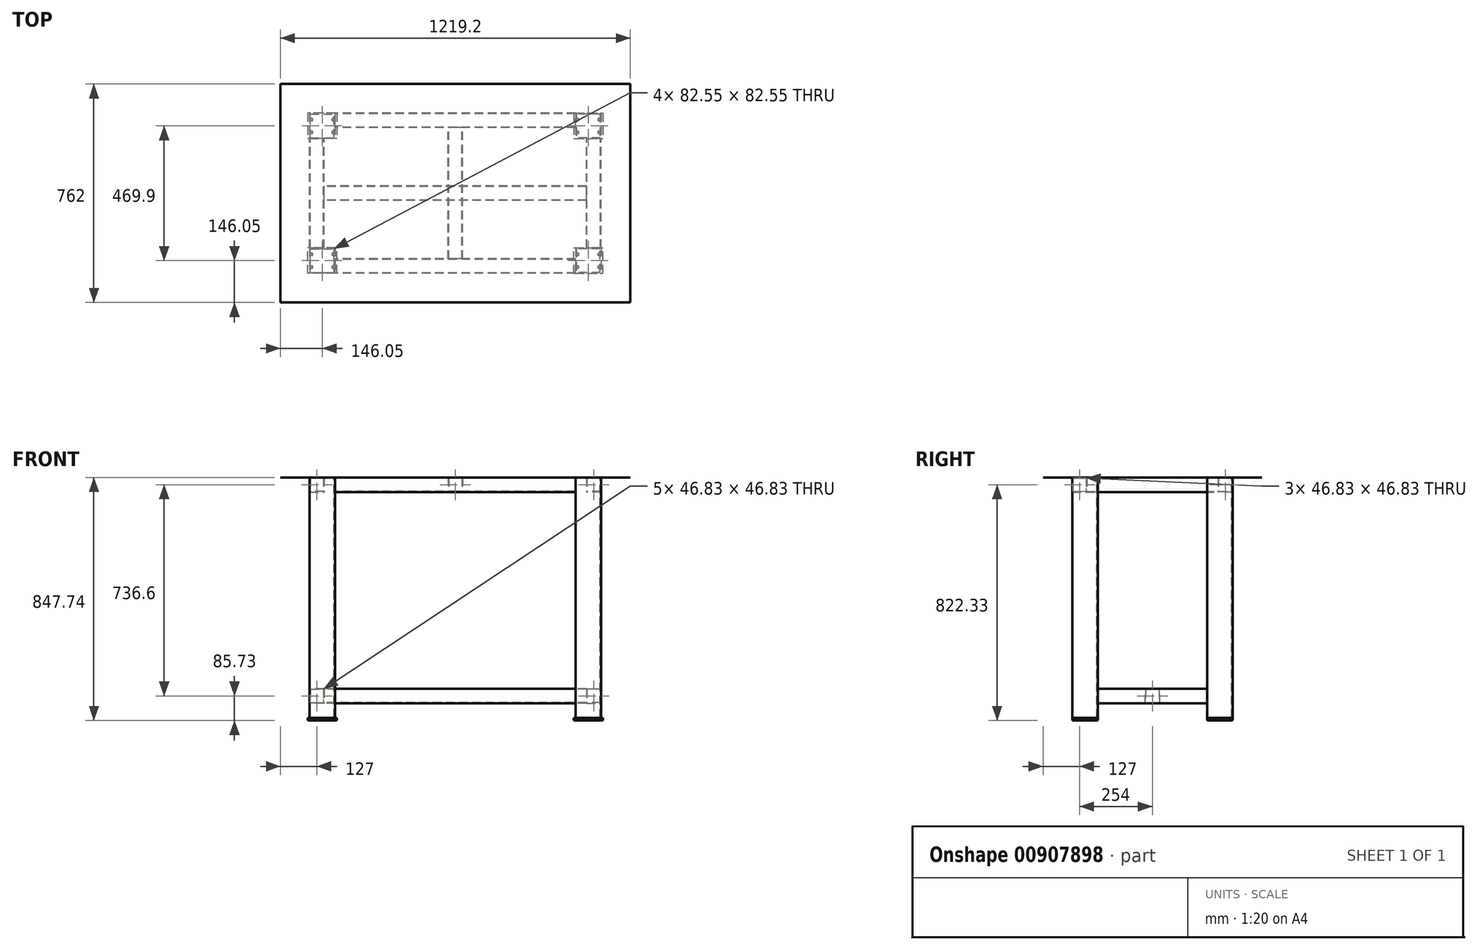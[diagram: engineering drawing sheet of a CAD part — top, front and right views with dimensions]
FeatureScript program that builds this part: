
annotation { "Feature Type Name" : "Feature", "Feature Type Description" : "" }
export const myFeature = defineFeature(function(context is Context, id is Id, definition is map)
    precondition{}
    {
        {
            var Q0;
            Q0=qCreatedBy(makeId("Top.planeOp"),FACE);
            var sketch = newSketch(context, id + "F0", { "sketchPlane" : qUnion([Q0])});
            skLineSegment(sketch, "E0.bottom", {"start": v(-419.1, 279.4) * mm, "end": v(-508, 279.4) * mm});
            skLineSegment(sketch, "E0.top", {"start": v(-419.1, 190.5) * mm, "end": v(-508, 190.5) * mm});
            skLineSegment(sketch, "E0.left", {"start": v(-419.1, 279.4) * mm, "end": v(-419.1, 190.5) * mm});
            skLineSegment(sketch, "E0.right", {"start": v(-508, 279.4) * mm, "end": v(-508, 190.5) * mm});
            skPoint(sketch, "E0.middle", {"position": v(-463.55, 234.95) * mm});
            skLineSegment(sketch, "E1.bottom", {"start": v(-419.1, -190.5) * mm, "end": v(-508, -190.5) * mm});
            skLineSegment(sketch, "E1.top", {"start": v(-419.1, -279.4) * mm, "end": v(-508, -279.4) * mm});
            skLineSegment(sketch, "E1.left", {"start": v(-419.1, -190.5) * mm, "end": v(-419.1, -279.4) * mm});
            skLineSegment(sketch, "E1.right", {"start": v(-508, -190.5) * mm, "end": v(-508, -279.4) * mm});
            skPoint(sketch, "E1.middle", {"position": v(-463.55, -234.95) * mm});
            skPoint(sketch, "E2.MirrorP", {"position": v(463.55, -234.95) * mm});
            skLineSegment(sketch, "E3.MirrorCS", {"start": v(419.1, 190.5) * mm, "end": v(508, 190.5) * mm});
            skLineSegment(sketch, "E4.MirrorCS", {"start": v(419.1, -190.5) * mm, "end": v(419.1, -279.4) * mm});
            skLineSegment(sketch, "E5.MirrorCS", {"start": v(419.1, 279.4) * mm, "end": v(419.1, 190.5) * mm});
            skLineSegment(sketch, "E6.MirrorCS", {"start": v(419.1, 279.4) * mm, "end": v(508, 279.4) * mm});
            skPoint(sketch, "E7.MirrorP", {"position": v(463.55, 234.95) * mm});
            skLineSegment(sketch, "E8.MirrorCS", {"start": v(419.1, -190.5) * mm, "end": v(508, -190.5) * mm});
            skLineSegment(sketch, "E9.MirrorCS", {"start": v(508, 279.4) * mm, "end": v(508, 190.5) * mm});
            skLineSegment(sketch, "E10.MirrorCS", {"start": v(419.1, -279.4) * mm, "end": v(508, -279.4) * mm});
            skLineSegment(sketch, "E11.MirrorCS", {"start": v(508, -190.5) * mm, "end": v(508, -279.4) * mm});
            skLineSegment(sketch, "E12.bottom", {"start": v(-504.83, 193.67) * mm, "end": v(-422.28, 193.67) * mm});
            skLineSegment(sketch, "E12.top", {"start": v(-504.83, 276.23) * mm, "end": v(-422.28, 276.23) * mm});
            skLineSegment(sketch, "E12.left", {"start": v(-504.83, 193.67) * mm, "end": v(-504.83, 276.23) * mm});
            skLineSegment(sketch, "E12.right", {"start": v(-422.28, 193.67) * mm, "end": v(-422.28, 276.23) * mm});
            skLineSegment(sketch, "E13.bottom", {"start": v(-504.83, -276.23) * mm, "end": v(-422.27, -276.23) * mm});
            skLineSegment(sketch, "E13.top", {"start": v(-504.83, -193.68) * mm, "end": v(-422.27, -193.68) * mm});
            skLineSegment(sketch, "E13.left", {"start": v(-504.83, -276.23) * mm, "end": v(-504.83, -193.68) * mm});
            skLineSegment(sketch, "E13.right", {"start": v(-422.27, -276.23) * mm, "end": v(-422.27, -193.68) * mm});
            skLineSegment(sketch, "E14.MirrorCS", {"start": v(-419.1, 190.5) * mm, "end": v(-419.1, 279.4) * mm});
            skLineSegment(sketch, "E15.MirrorCS", {"start": v(-504.83, 193.68) * mm, "end": v(-422.27, 193.68) * mm});
            skLineSegment(sketch, "E16.MirrorCS", {"start": v(-504.83, 276.23) * mm, "end": v(-422.27, 276.23) * mm});
            skLineSegment(sketch, "E17.MirrorCS", {"start": v(-504.83, 276.23) * mm, "end": v(-504.83, 193.68) * mm});
            skLineSegment(sketch, "E18.MirrorCS", {"start": v(-508, 190.5) * mm, "end": v(-508, 279.4) * mm});
            skLineSegment(sketch, "E19.MirrorCS", {"start": v(-422.27, 276.23) * mm, "end": v(-422.27, 193.68) * mm});
            skLineSegment(sketch, "E20.MirrorCS", {"start": v(-419.1, -279.4) * mm, "end": v(-419.1, -190.5) * mm});
            skLineSegment(sketch, "E21.MirrorCS", {"start": v(-422.28, -193.67) * mm, "end": v(-422.28, -276.23) * mm});
            skLineSegment(sketch, "E22.MirrorCS", {"start": v(504.83, 193.67) * mm, "end": v(422.28, 193.67) * mm});
            skLineSegment(sketch, "E23.MirrorCS", {"start": v(508, 190.5) * mm, "end": v(508, 279.4) * mm});
            skLineSegment(sketch, "E24.MirrorCS", {"start": v(422.28, -193.67) * mm, "end": v(422.28, -276.23) * mm});
            skLineSegment(sketch, "E25.MirrorCS", {"start": v(419.1, -279.4) * mm, "end": v(419.1, -190.5) * mm});
            skLineSegment(sketch, "E26.MirrorCS", {"start": v(504.83, 193.68) * mm, "end": v(422.27, 193.68) * mm});
            skLineSegment(sketch, "E27.MirrorCS", {"start": v(419.1, 190.5) * mm, "end": v(419.1, 279.4) * mm});
            skLineSegment(sketch, "E28.MirrorCS", {"start": v(504.83, -193.68) * mm, "end": v(422.27, -193.68) * mm});
            skLineSegment(sketch, "E29.MirrorCS", {"start": v(504.83, 276.23) * mm, "end": v(422.27, 276.23) * mm});
            skLineSegment(sketch, "E30.MirrorCS", {"start": v(422.27, -276.23) * mm, "end": v(422.27, -193.68) * mm});
            skLineSegment(sketch, "E31.MirrorCS", {"start": v(422.27, 276.23) * mm, "end": v(422.27, 193.68) * mm});
            skLineSegment(sketch, "E32.MirrorCS", {"start": v(504.83, 276.23) * mm, "end": v(504.83, 193.68) * mm});
            skLineSegment(sketch, "E33.MirrorCS", {"start": v(504.83, -276.23) * mm, "end": v(422.27, -276.23) * mm});
            skLineSegment(sketch, "E34.MirrorCS", {"start": v(422.28, 193.67) * mm, "end": v(422.28, 276.23) * mm});
            skLineSegment(sketch, "E35.MirrorCS", {"start": v(504.83, 193.67) * mm, "end": v(504.83, 276.23) * mm});
            skLineSegment(sketch, "E36.MirrorCS", {"start": v(504.83, 276.23) * mm, "end": v(422.28, 276.23) * mm});
            skLineSegment(sketch, "E37.MirrorCS", {"start": v(504.83, -276.23) * mm, "end": v(504.83, -193.68) * mm});
            skSolve(sketch);
        }
        {
            var Q0;
            Q0=makeQuery(id+"F0.imprint","IMPRINT",FACE,{"disambiguationData":[TD([[makeQuery(id+"F0.imprint","IMPRINT",EDGE,{"derivedFrom":sQuery(id+"F0.wireOp",EDGE,"E28.MirrorCS")}),-1.0]])]});
            var Q1;
            Q1=makeQuery(id+"F0.imprint","IMPRINT",FACE,{"disambiguationData":[TD([[makeQuery(id+"F0.imprint","IMPRINT",EDGE,{"derivedFrom":sQuery(id+"F0.wireOp",EDGE,"E26.MirrorCS")}),1.0]])]});
            var Q2;
            Q2=makeQuery(id+"F0.imprint","IMPRINT",FACE,{"disambiguationData":[TD([[makeQuery(id+"F0.imprint","IMPRINT",EDGE,{"derivedFrom":sQuery(id+"F0.wireOp",EDGE,"E1.top")}),-1.0]])]});
            var Q3;
            Q3=makeQuery(id+"F0.imprint","IMPRINT",FACE,{"disambiguationData":[TD([[makeQuery(id+"F0.imprint","IMPRINT",EDGE,{"derivedFrom":sQuery(id+"F0.wireOp",EDGE,"E15.MirrorCS")}),-1.0]])]});
            extrude(context, id + "F1", {"entities" : qUnion([Q0, Q1, Q2, Q3]), "oppositeDirection" : true, "depth" : 838.2 * mm, "offsetDistance" : 25.4 * mm});
        }
        {
            var Q0;
            Q0=qCreatedBy(makeId("Right.planeOp"),FACE);
            var sketch = newSketch(context, id + "F2", { "sketchPlane" : qUnion([Q0])});
            skLineSegment(sketch, "E38.bottom", {"start": v(-279.4, 0) * mm, "end": v(-228.6, 0) * mm});
            skLineSegment(sketch, "E38.top", {"start": v(-279.4, -50.8) * mm, "end": v(-228.6, -50.8) * mm});
            skLineSegment(sketch, "E38.left", {"start": v(-279.4, 0) * mm, "end": v(-279.4, -50.8) * mm});
            skLineSegment(sketch, "E38.right", {"start": v(-228.6, 0) * mm, "end": v(-228.6, -50.8) * mm});
            skLineSegment(sketch, "E39.bottom", {"start": v(279.4, 0) * mm, "end": v(228.6, 0) * mm});
            skLineSegment(sketch, "E39.top", {"start": v(279.4, -50.8) * mm, "end": v(228.6, -50.8) * mm});
            skLineSegment(sketch, "E39.left", {"start": v(228.6, 0) * mm, "end": v(228.6, -50.8) * mm});
            skLineSegment(sketch, "E39.right", {"start": v(279.4, 0) * mm, "end": v(279.4, -50.8) * mm});
            skLineSegment(sketch, "E40.bottom", {"start": v(230.58, -1.98) * mm, "end": v(277.42, -1.98) * mm});
            skLineSegment(sketch, "E40.top", {"start": v(230.58, -48.82) * mm, "end": v(277.42, -48.82) * mm});
            skLineSegment(sketch, "E40.left", {"start": v(230.58, -1.98) * mm, "end": v(230.58, -48.82) * mm});
            skLineSegment(sketch, "E40.right", {"start": v(277.42, -1.98) * mm, "end": v(277.42, -48.82) * mm});
            skPoint(sketch, "E40.middle", {"position": v(254, -25.4) * mm});
            skPoint(sketch, "E40.middle.positionSnap0", {"position": v(254, -50.8) * mm});
            skPoint(sketch, "E40.centerSnap0", {"position": v(254, -50.8) * mm});
            skLineSegment(sketch, "E41.bottom", {"start": v(-277.42, -1.98) * mm, "end": v(-230.58, -1.98) * mm});
            skLineSegment(sketch, "E41.top", {"start": v(-277.42, -48.82) * mm, "end": v(-230.58, -48.82) * mm});
            skLineSegment(sketch, "E41.left", {"start": v(-277.42, -1.98) * mm, "end": v(-277.42, -48.82) * mm});
            skLineSegment(sketch, "E41.right", {"start": v(-230.58, -1.98) * mm, "end": v(-230.58, -48.82) * mm});
            skPoint(sketch, "E41.middle", {"position": v(-254, -25.4) * mm});
            skPoint(sketch, "E41.middle.positionSnap0", {"position": v(-228.6, -25.4) * mm});
            skPoint(sketch, "E41.centerSnap0", {"position": v(-228.6, -25.4) * mm});
            skSolve(sketch);
        }
        {
            var Q0;
            Q0 = qSketchRegion(id + "F2", true);
            extrude(context, id + "F3", {"entities" : qUnion([Q0]), "depth" : 419.1 * mm, "offsetDistance" : 25.4 * mm, "hasSecondDirection" : true, "secondDirectionOppositeDirection" : true, "secondDirectionDepth" : 419.1 * mm});
        }
        {
            var Q0;
            Q0=qCreatedBy(makeId("Front.planeOp"),FACE);
            var sketch = newSketch(context, id + "F4", { "sketchPlane" : qUnion([Q0])});
            skLineSegment(sketch, "E42.bottom", {"start": v(-508, 0) * mm, "end": v(-457.2, 0) * mm});
            skLineSegment(sketch, "E42.top", {"start": v(-508, -50.8) * mm, "end": v(-457.2, -50.8) * mm});
            skLineSegment(sketch, "E42.left", {"start": v(-508, 0) * mm, "end": v(-508, -50.8) * mm});
            skLineSegment(sketch, "E42.right", {"start": v(-457.2, 0) * mm, "end": v(-457.2, -50.8) * mm});
            skLineSegment(sketch, "E43.bottom", {"start": v(508, 0) * mm, "end": v(457.2, 0) * mm});
            skLineSegment(sketch, "E43.top", {"start": v(508, -50.8) * mm, "end": v(457.2, -50.8) * mm});
            skLineSegment(sketch, "E43.left", {"start": v(508, 0) * mm, "end": v(508, -50.8) * mm});
            skLineSegment(sketch, "E43.right", {"start": v(457.2, 0) * mm, "end": v(457.2, -50.8) * mm});
            skLineSegment(sketch, "E44.bottom", {"start": v(-457.2, -736.6) * mm, "end": v(-508, -736.6) * mm});
            skLineSegment(sketch, "E44.top", {"start": v(-457.2, -787.4) * mm, "end": v(-508, -787.4) * mm});
            skLineSegment(sketch, "E44.left", {"start": v(-457.2, -736.6) * mm, "end": v(-457.2, -787.4) * mm});
            skLineSegment(sketch, "E44.right", {"start": v(-508, -736.6) * mm, "end": v(-508, -787.4) * mm});
            skLineSegment(sketch, "E45.bottom", {"start": v(457.2, -736.6) * mm, "end": v(508, -736.6) * mm});
            skLineSegment(sketch, "E45.top", {"start": v(457.2, -787.4) * mm, "end": v(508, -787.4) * mm});
            skLineSegment(sketch, "E45.left", {"start": v(457.2, -736.6) * mm, "end": v(457.2, -787.4) * mm});
            skLineSegment(sketch, "E45.right", {"start": v(508, -736.6) * mm, "end": v(508, -787.4) * mm});
            skLineSegment(sketch, "E46.bottom", {"start": v(-459.18, -1.98) * mm, "end": v(-506.02, -1.98) * mm});
            skLineSegment(sketch, "E46.top", {"start": v(-459.18, -48.82) * mm, "end": v(-506.02, -48.82) * mm});
            skLineSegment(sketch, "E46.left", {"start": v(-459.18, -1.98) * mm, "end": v(-459.18, -48.82) * mm});
            skLineSegment(sketch, "E46.right", {"start": v(-506.02, -1.98) * mm, "end": v(-506.02, -48.82) * mm});
            skPoint(sketch, "E46.middle", {"position": v(-482.6, -25.4) * mm});
            skPoint(sketch, "E46.middle.positionSnap0", {"position": v(-508, -25.4) * mm});
            skPoint(sketch, "E46.centerSnap0", {"position": v(-508, -25.4) * mm});
            skLineSegment(sketch, "E47.bottom", {"start": v(-506.02, -738.58) * mm, "end": v(-459.18, -738.58) * mm});
            skLineSegment(sketch, "E47.top", {"start": v(-506.02, -785.42) * mm, "end": v(-459.18, -785.42) * mm});
            skLineSegment(sketch, "E47.left", {"start": v(-506.02, -738.58) * mm, "end": v(-506.02, -785.42) * mm});
            skLineSegment(sketch, "E47.right", {"start": v(-459.18, -738.58) * mm, "end": v(-459.18, -785.42) * mm});
            skPoint(sketch, "E47.middle", {"position": v(-482.6, -762) * mm});
            skPoint(sketch, "E47.middle.positionSnap0", {"position": v(-457.2, -762) * mm});
            skPoint(sketch, "E47.centerSnap0", {"position": v(-457.2, -762) * mm});
            skLineSegment(sketch, "E48.bottom", {"start": v(506.02, -738.58) * mm, "end": v(459.18, -738.58) * mm});
            skLineSegment(sketch, "E48.top", {"start": v(506.02, -785.42) * mm, "end": v(459.18, -785.42) * mm});
            skLineSegment(sketch, "E48.left", {"start": v(506.02, -738.58) * mm, "end": v(506.02, -785.42) * mm});
            skLineSegment(sketch, "E48.right", {"start": v(459.18, -738.58) * mm, "end": v(459.18, -785.42) * mm});
            skPoint(sketch, "E48.middle", {"position": v(482.6, -762) * mm});
            skPoint(sketch, "E48.middle.positionSnap0", {"position": v(457.2, -762) * mm});
            skPoint(sketch, "E48.centerSnap0", {"position": v(457.2, -762) * mm});
            skLineSegment(sketch, "E49.bottom", {"start": v(506.02, -1.98) * mm, "end": v(459.18, -1.98) * mm});
            skLineSegment(sketch, "E49.top", {"start": v(506.02, -48.82) * mm, "end": v(459.18, -48.82) * mm});
            skLineSegment(sketch, "E49.left", {"start": v(506.02, -1.98) * mm, "end": v(506.02, -48.82) * mm});
            skLineSegment(sketch, "E49.right", {"start": v(459.18, -1.98) * mm, "end": v(459.18, -48.82) * mm});
            skPoint(sketch, "E49.middle", {"position": v(482.6, -25.4) * mm});
            skSolve(sketch);
        }
        {
            var Q0;
            Q0 = qSketchRegion(id + "F4", true);
            extrude(context, id + "F5", {"entities" : qUnion([Q0]), "depth" : 190.5 * mm, "offsetDistance" : 25.4 * mm, "hasSecondDirection" : true, "secondDirectionOppositeDirection" : true, "secondDirectionDepth" : 190.5 * mm});
        }
        {
            var Q0;
            Q0=qCreatedBy(makeId("Right.planeOp"),FACE);
            var sketch = newSketch(context, id + "F6", { "sketchPlane" : qUnion([Q0])});
            skLineSegment(sketch, "E50.bottom", {"start": v(-25.4, -787.4) * mm, "end": v(25.4, -787.4) * mm});
            skLineSegment(sketch, "E50.top", {"start": v(-25.4, -736.6) * mm, "end": v(25.4, -736.6) * mm});
            skLineSegment(sketch, "E50.left", {"start": v(-25.4, -787.4) * mm, "end": v(-25.4, -736.6) * mm});
            skLineSegment(sketch, "E50.right", {"start": v(25.4, -787.4) * mm, "end": v(25.4, -736.6) * mm});
            skLineSegment(sketch, "E51.bottom", {"start": v(-23.42, -738.58) * mm, "end": v(23.42, -738.58) * mm});
            skLineSegment(sketch, "E51.top", {"start": v(-23.42, -785.42) * mm, "end": v(23.42, -785.42) * mm});
            skLineSegment(sketch, "E51.left", {"start": v(-23.42, -738.58) * mm, "end": v(-23.42, -785.42) * mm});
            skLineSegment(sketch, "E51.right", {"start": v(23.42, -738.58) * mm, "end": v(23.42, -785.42) * mm});
            skPoint(sketch, "E51.middle", {"position": v(0, -762) * mm});
            skPoint(sketch, "E51.middle.positionSnap0", {"position": v(-25.4, -762) * mm});
            skPoint(sketch, "E51.centerSnap0", {"position": v(-25.4, -762) * mm});
            skSolve(sketch);
        }
        {
            var Q0;
            Q0=makeQuery(id+"F6.imprint","IMPRINT",FACE,{"disambiguationData":[TD([[makeQuery(id+"F6.imprint","IMPRINT",EDGE,{"derivedFrom":sQuery(id+"F6.wireOp",EDGE,"E50.bottom")}),1.0]])]});
            extrude(context, id + "F7", {"entities" : qUnion([Q0]), "depth" : 457.2 * mm, "offsetDistance" : 25.4 * mm, "hasSecondDirection" : true, "secondDirectionOppositeDirection" : true, "secondDirectionDepth" : 457.2 * mm});
        }
        {
            var Q0;
            Q0=qCreatedBy(makeId("Top.planeOp"),FACE);
            var sketch = newSketch(context, id + "F8", { "sketchPlane" : qUnion([Q0])});
            skLineSegment(sketch, "E52.bottom", {"start": v(609.6, -381) * mm, "end": v(-609.6, -381) * mm});
            skLineSegment(sketch, "E52.top", {"start": v(609.6, 381) * mm, "end": v(-609.6, 381) * mm});
            skLineSegment(sketch, "E52.left", {"start": v(609.6, -381) * mm, "end": v(609.6, 381) * mm});
            skLineSegment(sketch, "E52.right", {"start": v(-609.6, -381) * mm, "end": v(-609.6, 381) * mm});
            skPoint(sketch, "E52.middle", {"position": v(0, 0) * mm});
            skSolve(sketch);
        }
        {
            var Q0;
            Q0 = qSketchRegion(id + "F8", true);
            extrude(context, id + "F9", {"entities" : qUnion([Q0]), "depth" : 3 / 203.2 * mm, "offsetDistance" : 25.4 * mm});
        }
        {
            var Q0;
            Q0=makeQuery(id+"F1.opExtrude","CAP_FACE",FACE,{"disambiguationData":[OSD([sQuery(id+"F0.wireOp",EDGE,"E1.top"),sQuery(id+"F0.wireOp",EDGE,"E1.right"),sQuery(id+"F0.wireOp",EDGE,"E1.bottom"),sQuery(id+"F0.wireOp",EDGE,"E13.bottom"),sQuery(id+"F0.wireOp",EDGE,"E13.top"),sQuery(id+"F0.wireOp",EDGE,"E13.left"),sQuery(id+"F0.wireOp",EDGE,"E20.MirrorCS"),sQuery(id+"F0.wireOp",EDGE,"E21.MirrorCS")])],"isStart":false});
            cPlane(context, id + "F10", {"entities" : qUnion([Q0]), "cplaneType" : CPlaneType.OFFSET, "offset" : 0 * mm, "width" : 152.4 * mm, "height" : 152.4 * mm});
        }
        {
            var Q0;
            Q0=qCreatedBy(id+"F10.planeOp",FACE);
            var sketch = newSketch(context, id + "F11", { "sketchPlane" : qUnion([Q0])});
            skLineSegment(sketch, "E53.bottom", {"start": v(-412.75, 279.4) * mm, "end": v(-514.35, 279.4) * mm});
            skLineSegment(sketch, "E53.top", {"start": v(-412.75, 190.5) * mm, "end": v(-514.35, 190.5) * mm});
            skLineSegment(sketch, "E53.left", {"start": v(-412.75, 279.4) * mm, "end": v(-412.75, 190.5) * mm});
            skLineSegment(sketch, "E53.right", {"start": v(-514.35, 279.4) * mm, "end": v(-514.35, 190.5) * mm});
            skPoint(sketch, "E53.middle", {"position": v(-463.55, 234.95) * mm});
            skSolve(sketch);
        }
        {
            var Q0;
            Q0 = qSketchRegion(id + "F11", true);
            extrude(context, id + "F12", {"entities" : qUnion([Q0]), "depth" : 9.52 * mm, "offsetDistance" : 25.4 * mm});
        }
        {
            var Q0;
            Q0=makeQuery(id+"F12.opExtrude","CAP_FACE",FACE,{"disambiguationData":[OSD([sQuery(id+"F11.wireOp",EDGE,"E53.bottom"),sQuery(id+"F11.wireOp",EDGE,"E53.top"),sQuery(id+"F11.wireOp",EDGE,"E53.left"),sQuery(id+"F11.wireOp",EDGE,"E53.right")])],"isStart":false});
            cPlane(context, id + "F13", {"entities" : qUnion([Q0]), "cplaneType" : CPlaneType.OFFSET, "offset" : 0 * mm, "width" : 152.4 * mm, "height" : 152.4 * mm});
        }
        {
            var Q0;
            Q0=qCreatedBy(id+"F13.planeOp",FACE);
            var sketch = newSketch(context, id + "F14", { "sketchPlane" : qUnion([Q0])});
            skCircle(sketch, "E54", {"center": v(-427.04, 257.18) * mm, "radius": 4.76 * mm});
            skCircle(sketch, "E55", {"center": v(-427.04, 212.73) * mm, "radius": 4.76 * mm});
            skCircle(sketch, "E56", {"center": v(-500.06, 212.73) * mm, "radius": 4.76 * mm});
            skCircle(sketch, "E57", {"center": v(-500.06, 257.18) * mm, "radius": 4.76 * mm});
            skSolve(sketch);
        }
        {
            var Q0;
            Q0=sQuery(id+"F14.wireOp",VERTEX,"E57.center");
            var Q1;
            Q1=sQuery(id+"F14.wireOp",VERTEX,"E56.center");
            var Q2;
            Q2=sQuery(id+"F14.wireOp",VERTEX,"E55.center");
            var Q3;
            Q3=sQuery(id+"F14.wireOp",VERTEX,"E54.center");
            var Q4;
            Q4=makeQuery(id+"F1.opExtrude","SWEPT_BODY",BODY,{"disambiguationData":[OSD([sQuery(id+"F0.wireOp",EDGE,"E1.top"),sQuery(id+"F0.wireOp",EDGE,"E1.right"),sQuery(id+"F0.wireOp",EDGE,"E1.bottom"),sQuery(id+"F0.wireOp",EDGE,"E13.bottom"),sQuery(id+"F0.wireOp",EDGE,"E13.top"),sQuery(id+"F0.wireOp",EDGE,"E13.left"),sQuery(id+"F0.wireOp",EDGE,"E20.MirrorCS"),sQuery(id+"F0.wireOp",EDGE,"E21.MirrorCS")])]});
            var Q5;
            Q5=makeQuery(id+"F9.opExtrude","SWEPT_BODY",BODY,{"disambiguationData":[OSD([sQuery(id+"F8.wireOp",EDGE,"E52.bottom"),sQuery(id+"F8.wireOp",EDGE,"E52.top"),sQuery(id+"F8.wireOp",EDGE,"E52.left"),sQuery(id+"F8.wireOp",EDGE,"E52.right")])]});
            var Q6;
            Q6=makeQuery(id+"F12.opExtrude","SWEPT_BODY",BODY,{"disambiguationData":[OSD([sQuery(id+"F11.wireOp",EDGE,"E53.bottom"),sQuery(id+"F11.wireOp",EDGE,"E53.top"),sQuery(id+"F11.wireOp",EDGE,"E53.left"),sQuery(id+"F11.wireOp",EDGE,"E53.right")])]});
            hole(context, id + "F15", {"style" : HoleStyle.SIMPLE, "endStyle" : HoleEndStyle.BLIND, "standardTappedOrClearance" : lookupTablePath({ "standard" : "ANSI", "engagement" : "75%", "pitch" : "16 tpi", "size" : "3/8", "type" : "Tapped" }), "standardBlindInLast" : lookupTablePath({ "standard" : "ANSI", "engagement" : "75%", "pitch" : "16 tpi", "size" : "3/8", "type" : "Tapped" }), "holeDiameter" : 7.94 * mm, "majorDiameter" : 9.52 * mm, "showTappedDepth" : true, "holeDepth" : 9.52 * mm, "isTappedThrough" : true, "tappedDepth" : 4.76 * mm, "tapClearance" : 3, "locations" : qUnion([Q0, Q1, Q2, Q3]), "scope" : qUnion([Q4, Q5, Q6])});
        }
        {
            var Q0;
            Q0=makeQuery(id+"F12.opExtrude","SWEPT_BODY",BODY,{"disambiguationData":[OSD([sQuery(id+"F11.wireOp",EDGE,"E53.bottom"),sQuery(id+"F11.wireOp",EDGE,"E53.top"),sQuery(id+"F11.wireOp",EDGE,"E53.left"),sQuery(id+"F11.wireOp",EDGE,"E53.right")])]});
            var Q1;
            Q1=qCreatedBy(makeId("Front.planeOp"),FACE);
            mirror(context, id + "F16", {"entities" : qUnion([Q0]), "mirrorPlane" : qUnion([Q1])});
        }
        {
            var Q0;
            Q0=makeQuery(id+"F12.opExtrude","SWEPT_BODY",BODY,{"disambiguationData":[OSD([sQuery(id+"F11.wireOp",EDGE,"E53.bottom"),sQuery(id+"F11.wireOp",EDGE,"E53.top"),sQuery(id+"F11.wireOp",EDGE,"E53.left"),sQuery(id+"F11.wireOp",EDGE,"E53.right")])]});
            var Q1;
            Q1=makeQuery(id+"F16.opPattern","COPY",BODY,{"derivedFrom":makeQuery(id+"F12.opExtrude","SWEPT_BODY",BODY,{"disambiguationData":[OSD([sQuery(id+"F11.wireOp",EDGE,"E53.bottom"),sQuery(id+"F11.wireOp",EDGE,"E53.top"),sQuery(id+"F11.wireOp",EDGE,"E53.left"),sQuery(id+"F11.wireOp",EDGE,"E53.right")])]}),"instanceName":"1"});
            var Q2;
            Q2=qCreatedBy(makeId("Right.planeOp"),FACE);
            mirror(context, id + "F17", {"entities" : qUnion([Q0, Q1]), "mirrorPlane" : qUnion([Q2])});
        }
        {
            var Q0;
            Q0=qCreatedBy(makeId("Front.planeOp"),FACE);
            var sketch = newSketch(context, id + "F18", { "sketchPlane" : qUnion([Q0])});
            skLineSegment(sketch, "E58.bottom", {"start": v(25.4, 0) * mm, "end": v(-25.4, 0) * mm});
            skLineSegment(sketch, "E58.top", {"start": v(25.4, -50.8) * mm, "end": v(-25.4, -50.8) * mm});
            skLineSegment(sketch, "E58.left", {"start": v(25.4, 0) * mm, "end": v(25.4, -50.8) * mm});
            skLineSegment(sketch, "E58.right", {"start": v(-25.4, 0) * mm, "end": v(-25.4, -50.8) * mm});
            skPoint(sketch, "E58.middle", {"position": v(0, -25.4) * mm});
            skLineSegment(sketch, "E59.bottom", {"start": v(23.42, -1.98) * mm, "end": v(-23.42, -1.98) * mm});
            skLineSegment(sketch, "E59.top", {"start": v(23.42, -48.82) * mm, "end": v(-23.42, -48.82) * mm});
            skLineSegment(sketch, "E59.left", {"start": v(23.42, -1.98) * mm, "end": v(23.42, -48.82) * mm});
            skLineSegment(sketch, "E59.right", {"start": v(-23.42, -1.98) * mm, "end": v(-23.42, -48.82) * mm});
            skSolve(sketch);
        }
        {
            var Q0;
            Q0=makeQuery(id+"F18.imprint","IMPRINT",FACE,{"disambiguationData":[TD([[makeQuery(id+"F18.imprint","IMPRINT",EDGE,{"derivedFrom":sQuery(id+"F18.wireOp",EDGE,"E58.bottom")}),1.0]])]});
            extrude(context, id + "F19", {"entities" : qUnion([Q0]), "depth" : 228.6 * mm, "offsetDistance" : 25.4 * mm, "hasSecondDirection" : true, "secondDirectionOppositeDirection" : true, "secondDirectionDepth" : 228.6 * mm});
        }
    });
